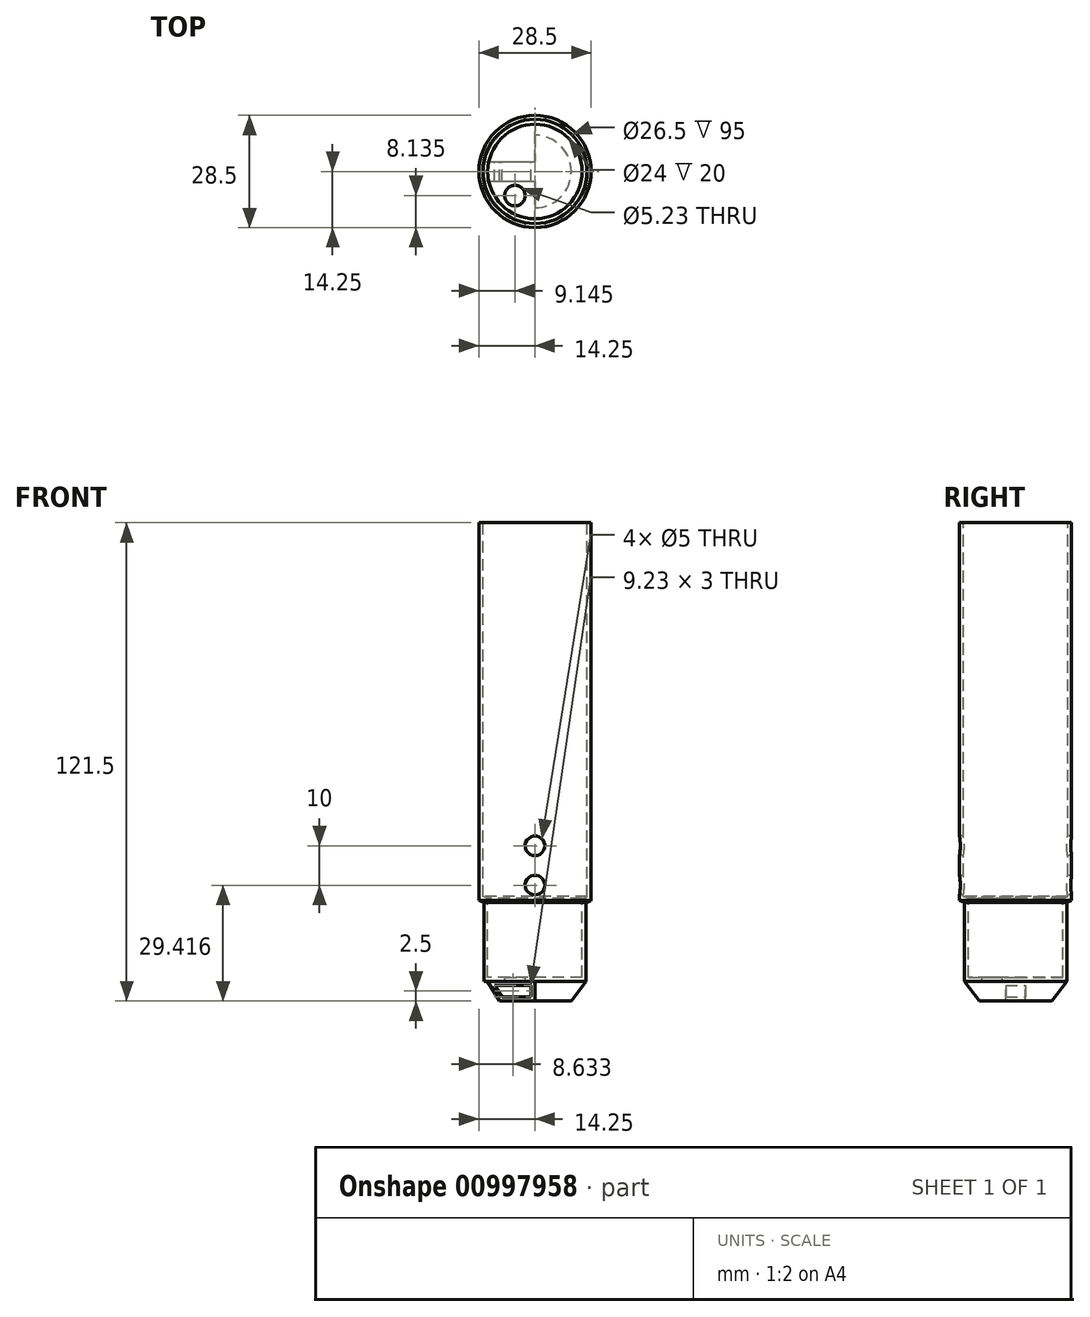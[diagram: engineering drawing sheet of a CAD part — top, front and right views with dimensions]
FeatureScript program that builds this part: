
annotation { "Feature Type Name" : "Feature", "Feature Type Description" : "" }
export const myFeature = defineFeature(function(context is Context, id is Id, definition is map)
    precondition{}
    {
        {
            var Q0;
            Q0=qCreatedBy(makeId("Front.planeOp"),FACE);
            var sketch = newSketch(context, id + "F0", { "sketchPlane" : qUnion([Q0])});
            skLineSegment(sketch, "E0", {"start": v(0, 0) * mm, "end": v(13, 0) * mm});
            skLineSegment(sketch, "E1", {"start": v(14.25, 20.5) * mm, "end": v(14.25, 116.5) * mm});
            skLineSegment(sketch, "E2", {"start": v(14.25, 116.5) * mm, "end": v(13.25, 116.5) * mm});
            skLineSegment(sketch, "E3", {"start": v(12, 21) * mm, "end": v(12, 1) * mm});
            skLineSegment(sketch, "E4", {"start": v(12, 1) * mm, "end": v(0, 1) * mm});
            skLineSegment(sketch, "E5", {"start": v(0, 1) * mm, "end": v(0, 0) * mm});
            skLineSegment(sketch, "E6", {"start": v(13, 0) * mm, "end": v(9.21, -5) * mm});
            skLineSegment(sketch, "E7", {"start": v(9.21, -5) * mm, "end": v(0, -5) * mm});
            skLineSegment(sketch, "E8", {"start": v(0, -5) * mm, "end": v(0, 0) * mm});
            skLineSegment(sketch, "E9", {"start": v(0, 0) * mm, "end": v(-13, 0) * mm, "construction": true});
            skLineSegment(sketch, "E10", {"start": v(-9, -5) * mm, "end": v(0, -5) * mm});
            skLineSegment(sketch, "E11", {"start": v(-13, 0) * mm, "end": v(-12, 0) * mm, "construction": true});
            skLineSegment(sketch, "E12", {"start": v(-12, 0) * mm, "end": v(-9, -5) * mm});
            skLineSegment(sketch, "E13", {"start": v(-12, 0) * mm, "end": v(0, 0) * mm});
            skLineSegment(sketch, "E14.0", {"start": v(-10.23, -1) * mm, "end": v(-1, -1) * mm});
            skLineSegment(sketch, "E14.1", {"start": v(-10.23, -1) * mm, "end": v(-8.43, -4) * mm});
            skLineSegment(sketch, "E14.2", {"start": v(-8.43, -4) * mm, "end": v(-1, -4) * mm});
            skLineSegment(sketch, "E14.3", {"start": v(-1, -4) * mm, "end": v(-1, -1) * mm});
            skLineSegment(sketch, "E15", {"start": v(13, 0) * mm, "end": v(13, 20) * mm});
            skLineSegment(sketch, "E16", {"start": v(13, 20) * mm, "end": v(14.25, 20.5) * mm});
            skLineSegment(sketch, "E17", {"start": v(13.25, 21.5) * mm, "end": v(12, 21) * mm});
            skLineSegment(sketch, "E18", {"start": v(13.25, 116.5) * mm, "end": v(13.25, 21.5) * mm});
            skSolve(sketch);
        }
        {
            var Q0;
            Q0=makeQuery(id+"F0.imprint","IMPRINT",FACE,{"disambiguationData":[TD([[makeQuery(id+"F0.imprint","IMPRINT",EDGE,{"derivedFrom":sQuery(id+"F0.wireOp",EDGE,"E0")}),1.0]])]});
            var Q1;
            Q1=sQuery(id+"F0.wireOp",EDGE,"E5");
            revolve(context, id + "F1", {"surfaceOperationType" : NewSurfaceOperationType.NEW, "entities" : qUnion([Q0]), "axis" : qUnion([Q1]), "revolveType" : RevolveType.FULL});
        }
        {
            var Q0;
            Q0=makeQuery(id+"F0.imprint","IMPRINT",FACE,{"disambiguationData":[TD([[makeQuery(id+"F0.imprint","IMPRINT",EDGE,{"derivedFrom":sQuery(id+"F0.wireOp",EDGE,"E0")}),-1.0]])]});
            var Q1;
            Q1=sQuery(id+"F0.wireOp",EDGE,"E8");
            revolve(context, id + "F2", {"operationType" : NewBodyOperationType.ADD, "surfaceOperationType" : NewSurfaceOperationType.NEW, "entities" : qUnion([Q0]), "axis" : qUnion([Q1]), "revolveType" : RevolveType.SYMMETRIC, "angle" : 180 * degree});
        }
        {
            var Q0;
            Q0=makeQuery(id+"F0.imprint","IMPRINT",FACE,{"disambiguationData":[TD([[makeQuery(id+"F0.imprint","IMPRINT",EDGE,{"derivedFrom":sQuery(id+"F0.wireOp",EDGE,"E8")}),1.0]])]});
            extrude(context, id + "F3", {"entities" : qUnion([Q0]), "operationType" : NewBodyOperationType.ADD, "endBound" : BoundingType.SYMMETRIC, "depth" : 5 * mm, "offsetDistance" : 25 * mm});
        }
        {
            var Q0;
            Q0=makeQuery(id+"F1.opRevolve","SWEPT_FACE",FACE,{"disambiguationData":[OSD([sQuery(id+"F0.wireOp",EDGE,"E0")])]});
            var sketch = newSketch(context, id + "F4", { "sketchPlane" : qUnion([Q0])});
            skCircle(sketch, "E19", {"center": v(-5.1, 6.12) * mm, "radius": 2.62 * mm});
            skSolve(sketch);
        }
        {
            var Q0;
            Q0 = qSketchRegion(id + "F4", true);
            extrude(context, id + "F5", {"entities" : qUnion([Q0]), "operationType" : NewBodyOperationType.REMOVE, "oppositeDirection" : true, "depth" : 25 * mm, "offsetDistance" : 25 * mm});
        }
        {
            var Q0;
            Q0=qCreatedBy(makeId("Front.planeOp"),FACE);
            var sketch = newSketch(context, id + "F6", { "sketchPlane" : qUnion([Q0])});
            skCircle(sketch, "E20", {"center": v(0, 24.42) * mm, "radius": 2.5 * mm});
            skCircle(sketch, "E21", {"center": v(0, 34.42) * mm, "radius": 2.5 * mm});
            skSolve(sketch);
        }
        {
            var Q0;
            Q0=makeQuery(id+"F6.imprint","IMPRINT",FACE,{"disambiguationData":[TD([[makeQuery(id+"F6.imprint","IMPRINT",EDGE,{"derivedFrom":sQuery(id+"F6.wireOp",EDGE,"E21")}),1.0]])]});
            var Q1;
            Q1=makeQuery(id+"F6.imprint","IMPRINT",FACE,{"disambiguationData":[TD([[makeQuery(id+"F6.imprint","IMPRINT",EDGE,{"derivedFrom":sQuery(id+"F6.wireOp",EDGE,"E20")}),1.0]])]});
            var Q2;
            Q2=sQuery(id+"F6.wireOp",EDGE,"E21");
            var Q3;
            Q3=sQuery(id+"F6.wireOp",EDGE,"E20");
            extrude(context, id + "F7", {"entities" : qUnion([Q0, Q1]), "operationType" : NewBodyOperationType.REMOVE, "surfaceEntities" : qUnion([Q2, Q3]), "endBound" : BoundingType.SYMMETRIC, "oppositeDirection" : true, "depth" : 50 * mm, "offsetDistance" : 25 * mm});
        }
    });
